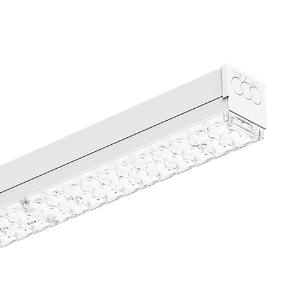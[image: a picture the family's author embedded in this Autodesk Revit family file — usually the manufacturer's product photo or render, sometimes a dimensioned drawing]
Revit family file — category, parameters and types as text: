
# Revit family: 3f_filippi_-_3f_zeta_l_3f_filippi_-_10988_-_3f_zeta_l_40_led_ep_l1489
name_source: partatom
category: Lighting Fixtures
units: mm (PartAtom-declared; Revit-internal decimal feet)

## family parameters
Cut with Voids When Loaded = No
Host = Face
Light Source = No
Part Type = Normal
Room Calculation Point = No
Round Connector Dimension = Use Diameter
Shared = No

## types (1)
- 3F Filippi - 3F Zeta L (1 x LED, 6872 lm, 40 W, 4000 K)
    Apparent Load = 40 VA
    Approval mark = ENEC
    CIE Flux Codes = 61 95 99 99 100
    Color Rendering = 80
    Color Temperature = 4000 K
    Control Gear = Electronic ballast
    Default Elevation = 1800 mm
    Description = ILLUMINOTECHNICAL
Luminous efficiency 100% (DLOR 99%, ULOR 1%).
Initial luminous flux of the luminaire 6872 lm.
Emergency luminaire luminous flux BLF 10.8%.
Direct symmetric distribution.
Installation Interdistance Transv.D = 1.39 x hu - Long.D = 1.43 x hu.
Tabular UGR (CIE 117 - 4H-8H; S=0.25H; 70/50/20): RUG 21.7 - 22.4.
Beam angle: 102° - 103°.
Luminous efficacy 172 lm/W.
Lifetime (L93/B10): 30000 h. (tq+25°C)
Lifetime (L90/B10): 50000 h. (tq+25°C)
Lifetime (L85/B10): 80000 h. (tq+25°C)
Lifetime (L80/B10): 100000 h. (tq+25°C)
Sudden decreased luminous flux after 50000 hours: 0% (C0).
Photobiological safety in compliance with IEC/TR 62778: RG0 risk exempt, (IEC 62471).
In compliance with IEC/EN 62722-2-1 - IEC/EN 62717 standards.

SOURCE
Linear LED module 40W/840.
Energy efficiency class (UE 2019/2020 - UE 2019/2015): C.
CIE 13.3 Colour rendering index: CRI >80 (R9 <50%).
IES TM-30 Fidelity Index: Rf = 84 Rg = 95.
CCT nominal colour temperature 4000 K.
Colour initial tolerance (MacAdam): SDCM 3.

MECHANICAL
Housing in hot-galvanised steel, painted in white polyester, obtained through rolling process.
Light unit in hot-galvanised steel, painted in white polyester base with fixing springs and retractable safety hooks in stainless steel.
Lenses for wide distribution, in transparent methacrylate (PMMA) with external flat surface.
End caps in white polycarbonate.
Pair of stainless steel sliding brackets with sliding block screws.
Luminaire with limited surface temperature. - D - (EN 60598-2-24)
Dimensions: 1489x62 mm, height 65 mm. Weight 4.56 kg.
IP40 protection degree.
Mechanical strength to impacts IK06 (1 joule).
Glow-wire test resistance 650°C.

ELECTRICAL
Halogen Free electronic wiring 230V-50/60Hz, power factor 0.90, THD <25%, constant output current, class I, 1 driver.
Power of the luminaire 40 W.
CE - IEC 60598-1 - EN 60598-1.
EP maintained emergency wiring on board, 1h duration, 24h recharge; compliant with EN 60598-2-22, excluding high risk areas.
SAFE FLICKER: PstLM=<1 and SVM=<0.4 (IEC TR 61547-1 and IEC TR 63158), to ensure a more comfortable and safe light.
Ambient temperature from +5°C to +25°C.
Temperature class T6 max 85°C.
Relative humidity UR: <85%.

INSTALLATION
Ceiling / Suspended / Wall.
All accessories dedicated to this product are available on the Catalog and on our website www.3F-Filippi.com.

APPLICATIONS
Suitable product for food production plants (HACCP), IFS (Food Version 6), BRC (GSFS Food Version 7).
In commercial environments, exhibition areas, shops and stores.

WARNING
Luminaire designed for disposal/recycling at end-of-life.
Replaceable (LED only) light source by a professional. Replaceable control gear by a professional.
    Height = 65 mm
    Lamp = 1 x LED
    Lamp Light Flux = 6872 lm
    Lamp Power = 40 W
    Lamp count = 1
    Length = 1489 mm
    Lifetime = 50000 h
    Luminous efficacy = 172 lm/W
    Manufacturer = 3F Filippi
    ModVariant = No
    Model = 3F Filippi - 10988 - 3F Zeta L 40 LED EP L1489
    Mounting Place = Ceiling
    Mounting Type = Pendant
    Number of Poles = 1
    OnlyDefault = Yes
    Power Factor = 1
    Product Name = 3F Filippi - 3F Zeta L
    Product group = pendant luminaire
    ProductGroupID = 9
    Protection Class = Protection class I
    Protection Degree = IP 40
    RLX_Detail_Level = 1
    RLX_Emergency_Light_Flux = 0 lm
    RLX_Emergency_Type = 0
    RLX_Emergency_Type_DB = No
    RlxData = <blob elided: 37085 chars, md5=27f460a1>
    Socket = socket
    Standby Power = 0 W
    System Light Flux = 6872 lm
    System Power = 40 W
    Type Comments = Product without accessories
    Type Image = 3ffilippi_3f_zeta_l.jpg
    URL = http://relux.com
    VarID = ---
    Voltage = 0 V
    Weight = 0.00 kg
    Width = 62 mm  [stored 0.203412 ft]

note: [stored X ft] marks values corroborated as IEEE doubles in the binary element streams (Revit-internal decimal feet)

## geometry (parser evidence)
native form markers: Blend x4, Sweep x10
no freeform markers — native parametric forms only
